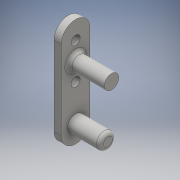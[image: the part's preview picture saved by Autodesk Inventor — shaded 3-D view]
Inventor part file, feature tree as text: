
AUTODESK INVENTOR PART (.ipt)
format: ipt  version: 2016 (Build 200138000, 138)  size: 148,480 bytes
history: native  units: mm
features: extrude x3, sketch x3, fillet x2
ambient origin geometry x8: Origin, YZ Plane, XZ Plane, XY Plane, X Axis, Y Axis, Z Axis, Center Point
bodies: Solid1 (feature_tree)
feature tree (8):
  extrude  "Extrusion1"  Depth=8.0mm
  extrude  "Extrusion2"  Depth=10.0mm
  fillet  "Fillet1"  Radius=5.0mm
  extrude  "Extrusion4"  Depth=1.0mm
  fillet  "Fillet2"  Radius=2.5mm
  sketch  "Sketch1"  dims[d0=30.0mm d1=8.0mm]
  sketch  "Sketch2"  dims[d2=10.0mm d3=20.0mm d4=5.0mm]
  sketch  "Sketch4"  dims[d5=4.5mm d6=2.5mm d7=2.5mm d8=4.0mm d9=2.0mm d10=0.0mm d11=4.0mm d12=5.0mm d13=10.0mm d14=0.0mm d19=1.0mm d20=9.0mm d21=2.0mm d22=0.0mm d23=0.0mm d24=1.0mm d25=4.8mm]
